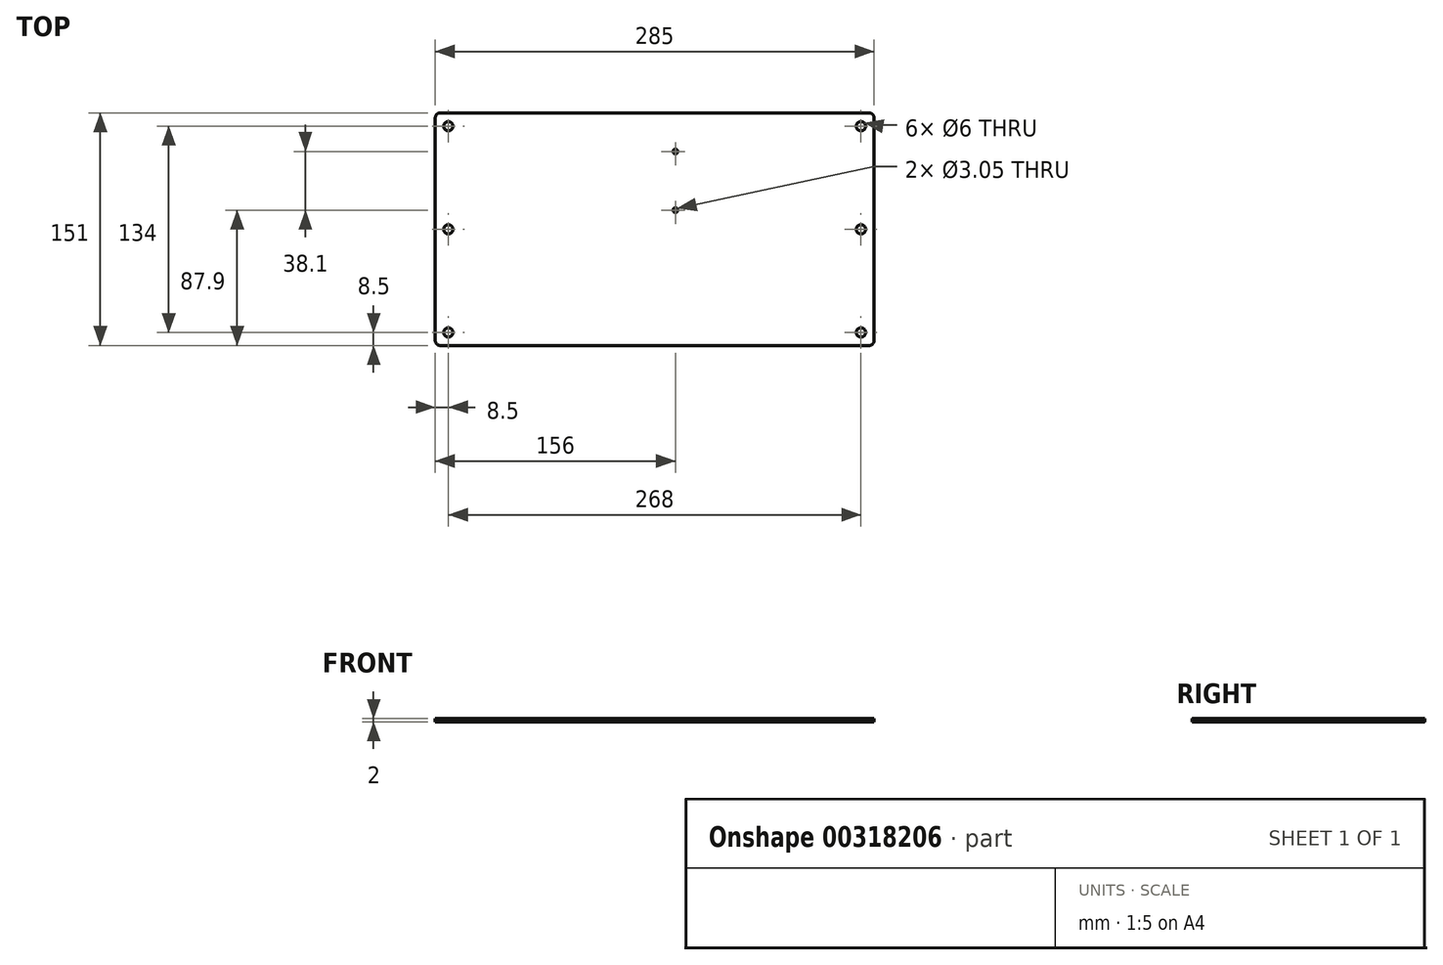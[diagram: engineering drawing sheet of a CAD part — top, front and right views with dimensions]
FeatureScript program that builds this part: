
annotation { "Feature Type Name" : "Feature", "Feature Type Description" : "" }
export const myFeature = defineFeature(function(context is Context, id is Id, definition is map)
    precondition{}
    {
        {
            var Q0;
            Q0=qCreatedBy(makeId("Top.planeOp"),FACE);
            var sketch = newSketch(context, id + "F0", { "sketchPlane" : qUnion([Q0])});
            skLineSegment(sketch, "E0.bottom", {"start": v(3, 0) * mm, "end": v(282, 0) * mm});
            skLineSegment(sketch, "E0.top", {"start": v(3, -151) * mm, "end": v(282, -151) * mm});
            skLineSegment(sketch, "E0.left", {"start": v(0, -3) * mm, "end": v(0, -148) * mm});
            skLineSegment(sketch, "E0.right", {"start": v(285, -3) * mm, "end": v(285, -148) * mm});
            skPoint(sketch, "E1.visualSharp", {"position": v(0, 0) * mm});
            skArc(sketch, "E1.filletArc", {"start": v(3, 0) * mm, "mid": v(0.88, -0.88) * mm, "end": v(0, -3) * mm});
            skPoint(sketch, "E2.visualSharp", {"position": v(285, 0) * mm});
            skArc(sketch, "E2.filletArc", {"start": v(285, -3) * mm, "mid": v(284.12, -0.88) * mm, "end": v(282, 0) * mm});
            skPoint(sketch, "E3.visualSharp", {"position": v(0, -151) * mm});
            skArc(sketch, "E3.filletArc", {"start": v(0, -148) * mm, "mid": v(0.88, -150.12) * mm, "end": v(3, -151) * mm});
            skPoint(sketch, "E4.visualSharp", {"position": v(285, -151) * mm});
            skArc(sketch, "E4.filletArc", {"start": v(282, -151) * mm, "mid": v(284.12, -150.12) * mm, "end": v(285, -148) * mm});
            skSolve(sketch);
        }
        {
            var Q0;
            Q0=makeQuery(id+"F0.imprint","IMPRINT",FACE,{"disambiguationData":[TD([[makeQuery(id+"F0.imprint","IMPRINT",EDGE,{"derivedFrom":sQuery(id+"F0.wireOp",EDGE,"E0.bottom")}),-1.0]])]});
            extrude(context, id + "F1", {"entities" : qUnion([Q0]), "depth" : 2 * mm});
        }
        {
            var Q0;
            Q0=makeQuery(id+"F1.opExtrude","CAP_FACE",FACE,{"disambiguationData":[OSD([sQuery(id+"F0.wireOp",EDGE,"E0.bottom"),sQuery(id+"F0.wireOp",EDGE,"E0.top"),sQuery(id+"F0.wireOp",EDGE,"E0.left"),sQuery(id+"F0.wireOp",EDGE,"E0.right"),sQuery(id+"F0.wireOp",EDGE,"E1.filletArc"),sQuery(id+"F0.wireOp",EDGE,"E2.filletArc"),sQuery(id+"F0.wireOp",EDGE,"E3.filletArc"),sQuery(id+"F0.wireOp",EDGE,"E4.filletArc")])],"isStart":false});
            var sketch = newSketch(context, id + "F2", { "sketchPlane" : qUnion([Q0])});
            skLineSegment(sketch, "E5", {"start": v(0, -75.5) * mm, "end": v(285, -75.5) * mm, "construction": true});
            skLineSegment(sketch, "E6", {"start": v(142.5, 0) * mm, "end": v(142.5, -151) * mm, "construction": true});
            skLineSegment(sketch, "E7.bottom", {"start": v(8.5, -8.5) * mm, "end": v(276.5, -8.5) * mm, "construction": true});
            skLineSegment(sketch, "E7.top", {"start": v(8.5, -142.5) * mm, "end": v(276.5, -142.5) * mm, "construction": true});
            skLineSegment(sketch, "E7.left", {"start": v(8.5, -8.5) * mm, "end": v(8.5, -142.5) * mm, "construction": true});
            skLineSegment(sketch, "E7.right", {"start": v(276.5, -8.5) * mm, "end": v(276.5, -142.5) * mm, "construction": true});
            skCircle(sketch, "E8", {"center": v(8.5, -8.5) * mm, "radius": 3 * mm});
            skCircle(sketch, "E9", {"center": v(276.5, -8.5) * mm, "radius": 3 * mm});
            skCircle(sketch, "E10", {"center": v(276.5, -75.5) * mm, "radius": 3 * mm});
            skCircle(sketch, "E11", {"center": v(276.5, -142.5) * mm, "radius": 3 * mm});
            skCircle(sketch, "E12", {"center": v(8.5, -142.5) * mm, "radius": 3 * mm});
            skCircle(sketch, "E13", {"center": v(8.5, -75.5) * mm, "radius": 3 * mm});
            skSolve(sketch);
        }
        {
            var Q0;
            Q0=makeQuery(id+"F2.imprint","IMPRINT",FACE,{"disambiguationData":[TD([[makeQuery(id+"F2.imprint","IMPRINT",EDGE,{"derivedFrom":sQuery(id+"F2.wireOp",EDGE,"E8")}),1.0]])]});
            var Q1;
            Q1=makeQuery(id+"F2.imprint","IMPRINT",FACE,{"disambiguationData":[TD([[makeQuery(id+"F2.imprint","IMPRINT",EDGE,{"derivedFrom":sQuery(id+"F2.wireOp",EDGE,"E13")}),1.0]])]});
            var Q2;
            Q2=makeQuery(id+"F2.imprint","IMPRINT",FACE,{"disambiguationData":[TD([[makeQuery(id+"F2.imprint","IMPRINT",EDGE,{"derivedFrom":sQuery(id+"F2.wireOp",EDGE,"E12")}),1.0]])]});
            var Q3;
            Q3=makeQuery(id+"F2.imprint","IMPRINT",FACE,{"disambiguationData":[TD([[makeQuery(id+"F2.imprint","IMPRINT",EDGE,{"derivedFrom":sQuery(id+"F2.wireOp",EDGE,"E11")}),1.0]])]});
            var Q4;
            Q4=makeQuery(id+"F2.imprint","IMPRINT",FACE,{"disambiguationData":[TD([[makeQuery(id+"F2.imprint","IMPRINT",EDGE,{"derivedFrom":sQuery(id+"F2.wireOp",EDGE,"E10")}),1.0]])]});
            var Q5;
            Q5=makeQuery(id+"F2.imprint","IMPRINT",FACE,{"disambiguationData":[TD([[makeQuery(id+"F2.imprint","IMPRINT",EDGE,{"derivedFrom":sQuery(id+"F2.wireOp",EDGE,"E9")}),1.0]])]});
            extrude(context, id + "F3", {"entities" : qUnion([Q0, Q1, Q2, Q3, Q4, Q5]), "operationType" : NewBodyOperationType.REMOVE, "oppositeDirection" : true, "depth" : 2 * mm});
        }
        {
            var Q0;
            Q0=makeQuery(id+"F1.opExtrude","CAP_FACE",FACE,{"disambiguationData":[OSD([sQuery(id+"F0.wireOp",EDGE,"E0.bottom"),sQuery(id+"F0.wireOp",EDGE,"E0.top"),sQuery(id+"F0.wireOp",EDGE,"E0.left"),sQuery(id+"F0.wireOp",EDGE,"E0.right"),sQuery(id+"F0.wireOp",EDGE,"E1.filletArc"),sQuery(id+"F0.wireOp",EDGE,"E2.filletArc"),sQuery(id+"F0.wireOp",EDGE,"E3.filletArc"),sQuery(id+"F0.wireOp",EDGE,"E4.filletArc")])],"isStart":false});
            var sketch = newSketch(context, id + "F4", { "sketchPlane" : qUnion([Q0])});
            skLineSegment(sketch, "E14", {"start": v(156, -25) * mm, "end": v(156, -63.1) * mm, "construction": true});
            skLineSegment(sketch, "E15", {"start": v(156, -25) * mm, "end": v(0, -25) * mm, "construction": true});
            skLineSegment(sketch, "E16", {"start": v(156, -63.1) * mm, "end": v(0, -63.1) * mm, "construction": true});
            skCircle(sketch, "E17", {"center": v(156, -25) * mm, "radius": 1.53 * mm});
            skCircle(sketch, "E18", {"center": v(156, -63.1) * mm, "radius": 1.52 * mm});
            skSolve(sketch);
        }
        {
            var Q0;
            Q0=makeQuery(id+"F4.imprint","IMPRINT",FACE,{"disambiguationData":[TD([[makeQuery(id+"F4.imprint","IMPRINT",EDGE,{"derivedFrom":sQuery(id+"F4.wireOp",EDGE,"E18")}),1.0]])]});
            var Q1;
            Q1=makeQuery(id+"F4.imprint","IMPRINT",FACE,{"disambiguationData":[TD([[makeQuery(id+"F4.imprint","IMPRINT",EDGE,{"derivedFrom":sQuery(id+"F4.wireOp",EDGE,"E17")}),1.0]])]});
            extrude(context, id + "F5", {"entities" : qUnion([Q0, Q1]), "operationType" : NewBodyOperationType.REMOVE, "oppositeDirection" : true, "depth" : 2 * mm});
        }
    });
